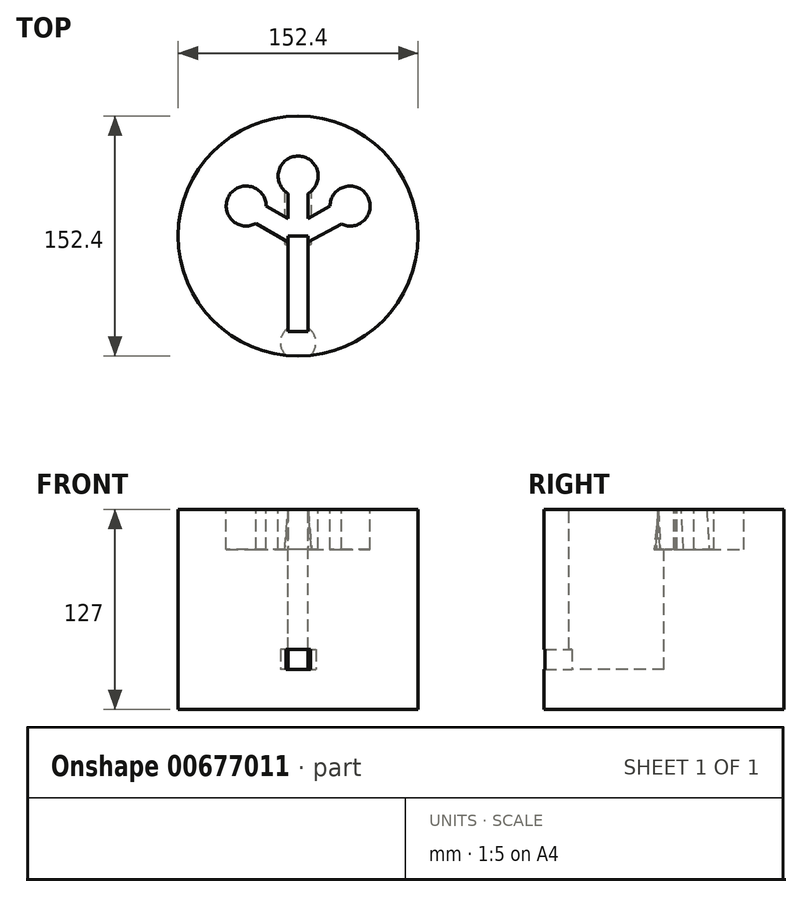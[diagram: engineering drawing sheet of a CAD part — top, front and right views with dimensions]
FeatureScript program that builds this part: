
annotation { "Feature Type Name" : "Feature", "Feature Type Description" : "" }
export const myFeature = defineFeature(function(context is Context, id is Id, definition is map)
    precondition{}
    {
        {
            var Q0;
            Q0=qCreatedBy(makeId("Top.planeOp"),FACE);
            var sketch = newSketch(context, id + "F0", { "sketchPlane" : qUnion([Q0])});
            skCircle(sketch, "E0", {"center": v(0, 0) * mm, "radius": 76.2 * mm});
            skSolve(sketch);
        }
        {
            var Q0;
            Q0=makeQuery(id+"F0.imprint","IMPRINT",FACE,{"disambiguationData":[TD([[makeQuery(id+"F0.imprint","IMPRINT",EDGE,{"derivedFrom":sQuery(id+"F0.wireOp",EDGE,"E0")}),1.0]])]});
            extrude(context, id + "F1", {"entities" : qUnion([Q0]), "depth" : 127 * mm, "offsetDistance" : 25.4 * mm});
        }
        {
            var Q0;
            Q0=makeQuery(id+"F1.opExtrude","CAP_FACE",FACE,{"disambiguationData":[OSD([sQuery(id+"F0.wireOp",EDGE,"E0")])],"isStart":false});
            cPlane(context, id + "F2", {"entities" : qUnion([Q0]), "cplaneType" : CPlaneType.OFFSET, "offset" : 101.6 * mm, "oppositeDirection" : true, "width" : 152.4 * mm, "height" : 152.4 * mm});
        }
        {
            var Q0;
            Q0=qCreatedBy(id+"F2.planeOp",FACE);
            var sketch = newSketch(context, id + "F3", { "sketchPlane" : qUnion([Q0])});
            skCircle(sketch, "E1", {"center": v(0, -67.7) * mm, "radius": 11.26 * mm});
            skSolve(sketch);
        }
        {
            var Q0;
            Q0=makeQuery(id+"F3.imprint","IMPRINT",FACE,{"disambiguationData":[TD([[makeQuery(id+"F3.imprint","IMPRINT",EDGE,{"derivedFrom":sQuery(id+"F3.wireOp",EDGE,"E1")}),1.0]])]});
            var Q1;
            Q1=sQuery(id+"F3.wireOp",EDGE,"E1");
            extrude(context, id + "F4", {"entities" : qUnion([Q0]), "operationType" : NewBodyOperationType.REMOVE, "surfaceEntities" : qUnion([Q1]), "depth" : 12.7 * mm, "offsetDistance" : 25.4 * mm});
        }
        {
            var Q0;
            Q0=makeQuery(id+"F1.opExtrude","CAP_FACE",FACE,{"disambiguationData":[OSD([sQuery(id+"F0.wireOp",EDGE,"E0")])],"isStart":false});
            cPlane(context, id + "F5", {"entities" : qUnion([Q0]), "cplaneType" : CPlaneType.OFFSET, "offset" : 0 * mm, "width" : 152.4 * mm, "height" : 152.4 * mm});
        }
        {
            var Q0;
            Q0=qCreatedBy(id+"F5.planeOp",FACE);
            var sketch = newSketch(context, id + "F6", { "sketchPlane" : qUnion([Q0])});
            skLineSegment(sketch, "E2", {"start": v(0, 0) * mm, "end": v(0, 38.1) * mm, "construction": true});
            skLineSegment(sketch, "E3", {"start": v(0, 0) * mm, "end": v(-33, 19.05) * mm, "construction": true});
            skPoint(sketch, "E3.endSnap0", {"position": v(0, 19.05) * mm});
            skLineSegment(sketch, "E4", {"start": v(0, 0) * mm, "end": v(33, 19.05) * mm, "construction": true});
            skLineSegment(sketch, "E5.bottom", {"start": v(6.35, 0) * mm, "end": v(-6.35, 0) * mm});
            skLineSegment(sketch, "E5.top", {"start": v(6.35, 38.1) * mm, "end": v(-6.35, 38.1) * mm});
            skLineSegment(sketch, "E5.left", {"start": v(6.35, 0) * mm, "end": v(6.35, 38.1) * mm});
            skLineSegment(sketch, "E5.right", {"start": v(-6.35, 0) * mm, "end": v(-6.35, 38.1) * mm});
            skLineSegment(sketch, "E6", {"start": v(-33, 19.05) * mm, "end": v(-29.82, 24.55) * mm});
            skLineSegment(sketch, "E7", {"start": v(-33, 19.05) * mm, "end": v(-36.17, 13.55) * mm});
            skLineSegment(sketch, "E8", {"start": v(0, 0) * mm, "end": v(3.18, 5.5) * mm});
            skLineSegment(sketch, "E9", {"start": v(0, 0) * mm, "end": v(-3.18, -5.5) * mm});
            skLineSegment(sketch, "E10", {"start": v(-36.17, 13.55) * mm, "end": v(-3.18, -5.5) * mm});
            skLineSegment(sketch, "E11", {"start": v(3.18, 5.5) * mm, "end": v(-29.82, 24.55) * mm});
            skLineSegment(sketch, "E12", {"start": v(33, 19.05) * mm, "end": v(36.66, 12.7) * mm});
            skLineSegment(sketch, "E13", {"start": v(33, 19.05) * mm, "end": v(29.82, 24.55) * mm});
            skLineSegment(sketch, "E14", {"start": v(0, 0) * mm, "end": v(3.18, -5.5) * mm});
            skLineSegment(sketch, "E15", {"start": v(0, 0) * mm, "end": v(-3.17, 5.5) * mm});
            skLineSegment(sketch, "E16", {"start": v(-3.18, 5.5) * mm, "end": v(29.82, 24.55) * mm});
            skLineSegment(sketch, "E17", {"start": v(3.17, -5.5) * mm, "end": v(36.66, 12.7) * mm});
            skCircle(sketch, "E18", {"center": v(-33, 19.05) * mm, "radius": 12.7 * mm});
            skCircle(sketch, "E19", {"center": v(0, 38.1) * mm, "radius": 12.7 * mm});
            skCircle(sketch, "E20", {"center": v(33, 19.05) * mm, "radius": 12.7 * mm});
            skLineSegment(sketch, "E21", {"start": v(-6.35, 0) * mm, "end": v(-6.35, -60.54) * mm});
            skLineSegment(sketch, "E22", {"start": v(6.35, 0) * mm, "end": v(6.35, -60.54) * mm});
            skLineSegment(sketch, "E23", {"start": v(6.35, -60.54) * mm, "end": v(-6.35, -60.54) * mm});
            skSolve(sketch);
        }
        {
            var Q0;
            {var subQ0=sQuery(id+"F6.wireOp",EDGE,"E5.top");Q0=makeQuery(id+"F6.imprint","IMPRINT",FACE,{"disambiguationData":[TD([[makeQuery(id+"F6.imprint","IMPRINT",EDGE,{"derivedFrom":subQ0}),-1.0]])]});}
            var Q1;
            {var subQ0=sQuery(id+"F6.wireOp",EDGE,"E5.top");Q1=makeQuery(id+"F6.imprint","IMPRINT",FACE,{"disambiguationData":[TD([[makeQuery(id+"F6.imprint","IMPRINT",EDGE,{"derivedFrom":subQ0}),1.0]])]});}
            var Q2;
            {var subQ1=sQuery(id+"F6.wireOp",EDGE,"E6");Q2=makeQuery(id+"F6.imprint","IMPRINT",FACE,{"disambiguationData":[TD([[makeQuery(id+"F6.imprint","IMPRINT",EDGE,{"derivedFrom":subQ1}),1.0]])]});}
            var Q3;
            {var subQ1=sQuery(id+"F6.wireOp",EDGE,"E12");Q3=makeQuery(id+"F6.imprint","IMPRINT",FACE,{"disambiguationData":[TD([[makeQuery(id+"F6.imprint","IMPRINT",EDGE,{"derivedFrom":subQ1}),1.0]])]});}
            var Q4;
            {var subQ1=sQuery(id+"F6.wireOp",EDGE,"E12");Q4=makeQuery(id+"F6.imprint","IMPRINT",FACE,{"disambiguationData":[TD([[makeQuery(id+"F6.imprint","IMPRINT",EDGE,{"derivedFrom":subQ1}),-1.0]])]});}
            var Q5;
            {var subQ1=sQuery(id+"F6.wireOp",EDGE,"E6");Q5=makeQuery(id+"F6.imprint","IMPRINT",FACE,{"disambiguationData":[TD([[makeQuery(id+"F6.imprint","IMPRINT",EDGE,{"derivedFrom":subQ1}),-1.0]])]});}
            var Q6;
            {var subQ0=sQuery(id+"F6.wireOp",EDGE,"E18");var subQ1=sQuery(id+"F6.wireOp",EDGE,"E10");var subQ2=makeQuery(id+"F6.imprint","INTERSECT",VERTEX,{"derivedFrom":[subQ1,subQ0]});Q6=makeQuery(id+"F6.imprint","IMPRINT",FACE,{"disambiguationData":[TD([[makeQuery(id+"F6.imprint","IMPRINT",EDGE,{"disambiguationData":[TD([[subQ2,-1.0]])],"derivedFrom":subQ1}),1.0]])]});}
            var Q7;
            {var subQ0=sQuery(id+"F6.wireOp",EDGE,"E15");Q7=makeQuery(id+"F6.imprint","IMPRINT",FACE,{"disambiguationData":[TD([[makeQuery(id+"F6.imprint","IMPRINT",EDGE,{"derivedFrom":subQ0}),1.0]])]});}
            var Q8;
            {var subQ0=sQuery(id+"F6.wireOp",EDGE,"E8");Q8=makeQuery(id+"F6.imprint","IMPRINT",FACE,{"disambiguationData":[TD([[makeQuery(id+"F6.imprint","IMPRINT",EDGE,{"derivedFrom":subQ0}),1.0]])]});}
            var Q9;
            {var subQ3=sQuery(id+"F6.wireOp",EDGE,"E9");Q9=makeQuery(id+"F6.imprint","IMPRINT",FACE,{"disambiguationData":[TD([[makeQuery(id+"F6.imprint","IMPRINT",EDGE,{"derivedFrom":subQ3}),-1.0]])]});}
            var Q10;
            {var subQ1=sQuery(id+"F6.wireOp",EDGE,"E16");var subQ7=sQuery(id+"F6.wireOp",EDGE,"E5.left");var subQ8=makeQuery(id+"F6.imprint","INTERSECT",VERTEX,{"derivedFrom":[subQ7,subQ1]});Q10=makeQuery(id+"F6.imprint","IMPRINT",FACE,{"disambiguationData":[TD([[makeQuery(id+"F6.imprint","IMPRINT",EDGE,{"disambiguationData":[TD([[subQ8,-1.0]])],"derivedFrom":subQ1}),-1.0]])]});}
            var Q11;
            {var subQ1=sQuery(id+"F6.wireOp",EDGE,"E8");Q11=makeQuery(id+"F6.imprint","IMPRINT",FACE,{"disambiguationData":[TD([[makeQuery(id+"F6.imprint","IMPRINT",EDGE,{"derivedFrom":subQ1}),-1.0]])]});}
            var Q12;
            {var subQ3=sQuery(id+"F6.wireOp",EDGE,"E14");Q12=makeQuery(id+"F6.imprint","IMPRINT",FACE,{"disambiguationData":[TD([[makeQuery(id+"F6.imprint","IMPRINT",EDGE,{"derivedFrom":subQ3}),1.0]])]});}
            extrude(context, id + "F7", {"entities" : qUnion([Q0, Q1, Q2, Q3, Q4, Q5, Q6, Q7, Q8, Q9, Q10, Q11, Q12]), "operationType" : NewBodyOperationType.REMOVE, "oppositeDirection" : true, "depth" : 25.4 * mm, "offsetDistance" : 25.4 * mm});
        }
        {
            var Q0;
            {var subQ0=sQuery(id+"F6.wireOp",EDGE,"E15");Q0=makeQuery(id+"F6.imprint","IMPRINT",FACE,{"disambiguationData":[TD([[makeQuery(id+"F6.imprint","IMPRINT",EDGE,{"derivedFrom":subQ0}),1.0]])]});}
            var Q1;
            {var subQ3=sQuery(id+"F6.wireOp",EDGE,"E16");var subQ7=sQuery(id+"F6.wireOp",EDGE,"E5.left");var subQ8=makeQuery(id+"F6.imprint","INTERSECT",VERTEX,{"derivedFrom":[subQ7,subQ3]});Q1=makeQuery(id+"F6.imprint","IMPRINT",FACE,{"disambiguationData":[TD([[makeQuery(id+"F6.imprint","IMPRINT",EDGE,{"disambiguationData":[TD([[subQ8,-1.0]])],"derivedFrom":subQ7}),1.0]])]});}
            var Q2;
            {var subQ1=sQuery(id+"F6.wireOp",EDGE,"E9");Q2=makeQuery(id+"F6.imprint","IMPRINT",FACE,{"disambiguationData":[TD([[makeQuery(id+"F6.imprint","IMPRINT",EDGE,{"derivedFrom":subQ1}),-1.0]])]});}
            var Q3;
            {var subQ0=sQuery(id+"F6.wireOp",EDGE,"E8");Q3=makeQuery(id+"F6.imprint","IMPRINT",FACE,{"disambiguationData":[TD([[makeQuery(id+"F6.imprint","IMPRINT",EDGE,{"derivedFrom":subQ0}),1.0]])]});}
            var Q4;
            {var subQ0=sQuery(id+"F6.wireOp",EDGE,"E14");Q4=makeQuery(id+"F6.imprint","IMPRINT",FACE,{"disambiguationData":[TD([[makeQuery(id+"F6.imprint","IMPRINT",EDGE,{"derivedFrom":subQ0}),1.0]])]});}
            var Q5;
            {var subQ0=sQuery(id+"F6.wireOp",EDGE,"E8");Q5=makeQuery(id+"F6.imprint","IMPRINT",FACE,{"disambiguationData":[TD([[makeQuery(id+"F6.imprint","IMPRINT",EDGE,{"derivedFrom":subQ0}),-1.0]])]});}
            extrude(context, id + "F8", {"entities" : qUnion([Q0, Q1, Q2, Q3, Q4, Q5]), "operationType" : NewBodyOperationType.REMOVE, "oppositeDirection" : true, "depth" : 25.4 * mm, "offsetDistance" : 25.4 * mm, "hasDraft" : true, "draftAngle" : 5 * degree});
        }
        {
            var Q0;
            {var subQ5=sQuery(id+"F6.wireOp",EDGE,"E9");Q0=makeQuery(id+"F6.imprint","IMPRINT",FACE,{"disambiguationData":[TD([[makeQuery(id+"F6.imprint","IMPRINT",EDGE,{"derivedFrom":subQ5}),1.0]])]});}
            var Q1;
            {var subQ3=sQuery(id+"F6.wireOp",EDGE,"E9");Q1=makeQuery(id+"F6.imprint","IMPRINT",FACE,{"disambiguationData":[TD([[makeQuery(id+"F6.imprint","IMPRINT",EDGE,{"derivedFrom":subQ3}),-1.0]])]});}
            var Q2;
            {var subQ3=sQuery(id+"F6.wireOp",EDGE,"E14");Q2=makeQuery(id+"F6.imprint","IMPRINT",FACE,{"disambiguationData":[TD([[makeQuery(id+"F6.imprint","IMPRINT",EDGE,{"derivedFrom":subQ3}),1.0]])]});}
            extrude(context, id + "F9", {"entities" : qUnion([Q0, Q1, Q2]), "operationType" : NewBodyOperationType.REMOVE, "oppositeDirection" : true, "depth" : 101.6 * mm, "offsetDistance" : 25.4 * mm});
        }
    });
